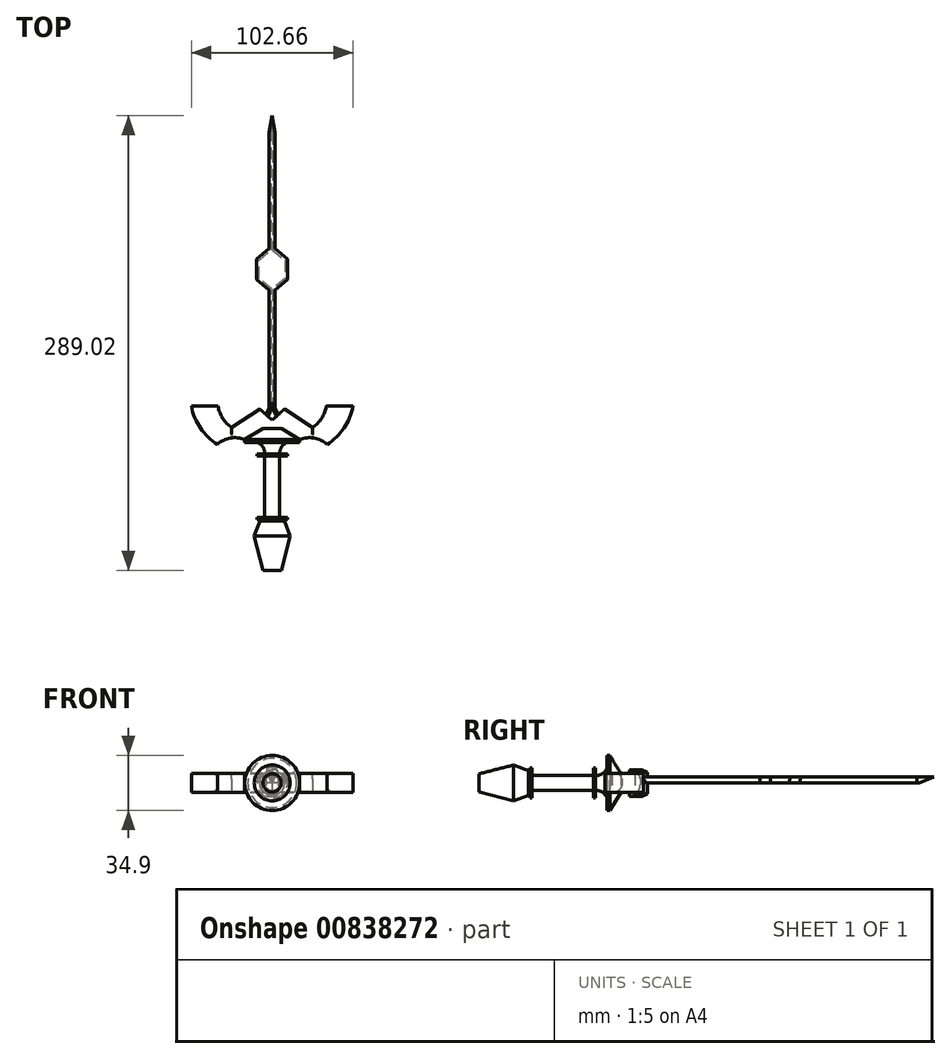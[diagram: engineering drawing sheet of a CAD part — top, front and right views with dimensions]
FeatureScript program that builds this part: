
annotation { "Feature Type Name" : "Feature", "Feature Type Description" : "" }
export const myFeature = defineFeature(function(context is Context, id is Id, definition is map)
    precondition{}
    {
        {
            var Q0;
            Q0=qCreatedBy(makeId("Top.planeOp"),FACE);
            var sketch = newSketch(context, id + "F0", { "sketchPlane" : qUnion([Q0])});
            skLineSegment(sketch, "E0", {"start": v(-11.37, -34.16) * mm, "end": v(-5.8, -56.21) * mm});
            skLineSegment(sketch, "E1", {"start": v(-5.8, -56.21) * mm, "end": v(0, -56.21) * mm});
            skLineSegment(sketch, "E2", {"start": v(-11.37, -34.16) * mm, "end": v(-7.82, -24.78) * mm});
            skLineSegment(sketch, "E3", {"start": v(-7.82, -24.78) * mm, "end": v(0, -24.78) * mm});
            skLineSegment(sketch, "E4", {"start": v(0, -24.78) * mm, "end": v(0, -56.21) * mm});
            skLineSegment(sketch, "E5", {"start": v(-11.37, -34.16) * mm, "end": v(0, -34.16) * mm});
            skLineSegment(sketch, "E6.top", {"start": v(-7.82, -23.73) * mm, "end": v(0, -23.73) * mm});
            skLineSegment(sketch, "E6.left", {"start": v(-7.82, -24.78) * mm, "end": v(-7.82, -23.73) * mm});
            skLineSegment(sketch, "E6.right", {"start": v(0, -24.78) * mm, "end": v(0, -23.73) * mm});
            skLineSegment(sketch, "E7.bottom", {"start": v(0, -23.73) * mm, "end": v(-9.63, -23.73) * mm});
            skLineSegment(sketch, "E7.top", {"start": v(0, -22.58) * mm, "end": v(-9.63, -22.58) * mm});
            skLineSegment(sketch, "E7.left", {"start": v(0, -23.73) * mm, "end": v(0, -22.58) * mm});
            skLineSegment(sketch, "E7.right", {"start": v(-9.63, -23.73) * mm, "end": v(-9.63, -22.58) * mm});
            skLineSegment(sketch, "E8.bottom", {"start": v(-4.82, -22.58) * mm, "end": v(0, -22.58) * mm});
            skLineSegment(sketch, "E8.top", {"start": v(-4.82, 16.66) * mm, "end": v(0, 16.66) * mm});
            skLineSegment(sketch, "E8.left", {"start": v(-4.82, -22.58) * mm, "end": v(-4.82, 16.66) * mm});
            skLineSegment(sketch, "E8.right", {"start": v(0, -22.58) * mm, "end": v(0, 16.66) * mm});
            skLineSegment(sketch, "E9.bottom", {"start": v(0, 16.66) * mm, "end": v(-9.63, 16.66) * mm});
            skLineSegment(sketch, "E9.top", {"start": v(0, 17.78) * mm, "end": v(-9.63, 17.78) * mm});
            skLineSegment(sketch, "E9.left", {"start": v(0, 16.66) * mm, "end": v(0, 17.78) * mm});
            skLineSegment(sketch, "E9.right", {"start": v(-9.63, 16.66) * mm, "end": v(-9.63, 17.78) * mm});
            skArc(sketch, "E10", {"start": v(-4.82, 17.78) * mm, "mid": v(-5.97, 22.28) * mm, "end": v(-9.63, 25.15) * mm});
            skLineSegment(sketch, "E11", {"start": v(0, 17.78) * mm, "end": v(0, 25.15) * mm});
            skLineSegment(sketch, "E12", {"start": v(0, 25.15) * mm, "end": v(-9.63, 25.15) * mm});
            skLineSegment(sketch, "E13.bottom", {"start": v(0, 25.15) * mm, "end": v(-17.45, 25.15) * mm});
            skLineSegment(sketch, "E13.top", {"start": v(0, 26.88) * mm, "end": v(-17.45, 26.88) * mm});
            skLineSegment(sketch, "E13.left", {"start": v(0, 25.15) * mm, "end": v(0, 26.88) * mm});
            skLineSegment(sketch, "E13.right", {"start": v(-17.45, 25.15) * mm, "end": v(-17.45, 26.88) * mm});
            skLineSegment(sketch, "E14", {"start": v(-5.94, 34.05) * mm, "end": v(0, 34.05) * mm});
            skLineSegment(sketch, "E15", {"start": v(0, 34.05) * mm, "end": v(0, 26.88) * mm});
            skArc(sketch, "E16", {"start": v(-17.45, 26.88) * mm, "mid": v(-26.6, 27.93) * mm, "end": v(-34.83, 23.84) * mm});
            skArc(sketch, "E17", {"start": v(-51.33, 48.17) * mm, "mid": v(-45.6, 34.3) * mm, "end": v(-34.83, 23.84) * mm});
            skLineSegment(sketch, "E18", {"start": v(-51.33, 48.17) * mm, "end": v(-34.4, 48.17) * mm});
            skArc(sketch, "E19", {"start": v(-34.4, 48.17) * mm, "mid": v(-31.41, 40.46) * mm, "end": v(-25.7, 34.49) * mm});
            skLineSegment(sketch, "E20", {"start": v(-25.7, 34.49) * mm, "end": v(-7.68, 46.21) * mm});
            skLineSegment(sketch, "E21", {"start": v(-7.68, 46.21) * mm, "end": v(0, 39.26) * mm});
            skLineSegment(sketch, "E22.MirrorCS", {"start": v(7.68, 46.21) * mm, "end": v(0, 39.26) * mm});
            skLineSegment(sketch, "E23.MirrorCS", {"start": v(25.7, 34.49) * mm, "end": v(7.68, 46.21) * mm});
            skLineSegment(sketch, "E24.MirrorCS", {"start": v(5.94, 34.05) * mm, "end": v(0, 34.05) * mm});
            skArc(sketch, "E25.MirrorCS", {"start": v(17.45, 26.88) * mm, "mid": v(26.6, 27.93) * mm, "end": v(34.83, 23.84) * mm});
            skArc(sketch, "E26.MirrorCS", {"start": v(51.33, 48.17) * mm, "mid": v(45.6, 34.3) * mm, "end": v(34.83, 23.84) * mm});
            skLineSegment(sketch, "E27.MirrorCS", {"start": v(51.33, 48.17) * mm, "end": v(34.4, 48.17) * mm});
            skArc(sketch, "E28.MirrorCS", {"start": v(34.4, 48.17) * mm, "mid": v(31.41, 40.46) * mm, "end": v(25.7, 34.49) * mm});
            skLineSegment(sketch, "E29", {"start": v(-7.68, 46.21) * mm, "end": v(-7.68, 119.1) * mm});
            skLineSegment(sketch, "E30", {"start": v(7.68, 46.21) * mm, "end": v(7.68, 119.1) * mm});
            skLineSegment(sketch, "E31", {"start": v(-7.68, 119.1) * mm, "end": v(-15.66, 125.77) * mm});
            skLineSegment(sketch, "E32", {"start": v(-15.66, 125.77) * mm, "end": v(-15.66, 144.25) * mm});
            skLineSegment(sketch, "E33", {"start": v(-15.66, 144.25) * mm, "end": v(-7.68, 150.92) * mm});
            skLineSegment(sketch, "E34", {"start": v(-7.68, 150.92) * mm, "end": v(-7.68, 222.52) * mm});
            skLineSegment(sketch, "E35", {"start": v(-7.68, 222.52) * mm, "end": v(0, 267.13) * mm});
            skLineSegment(sketch, "E36.MirrorCS", {"start": v(7.68, 119.1) * mm, "end": v(15.66, 125.77) * mm});
            skLineSegment(sketch, "E37.MirrorCS", {"start": v(15.66, 125.77) * mm, "end": v(15.66, 144.25) * mm});
            skLineSegment(sketch, "E38.MirrorCS", {"start": v(15.66, 144.25) * mm, "end": v(7.68, 150.92) * mm});
            skLineSegment(sketch, "E39.MirrorCS", {"start": v(7.68, 150.92) * mm, "end": v(7.68, 222.52) * mm});
            skLineSegment(sketch, "E40.MirrorCS", {"start": v(7.68, 222.52) * mm, "end": v(0, 267.13) * mm});
            skLineSegment(sketch, "E41", {"start": v(-5.94, 34.05) * mm, "end": v(-15.55, 26.88) * mm});
            skLineSegment(sketch, "E42.MirrorCS", {"start": v(5.94, 34.05) * mm, "end": v(15.55, 26.88) * mm});
            skLineSegment(sketch, "E43", {"start": v(15.55, 26.88) * mm, "end": v(17.45, 26.88) * mm});
            skLineSegment(sketch, "E44", {"start": v(-5.94, 34.05) * mm, "end": v(-17.45, 26.88) * mm});
            skLineSegment(sketch, "E45", {"start": v(5.94, 34.05) * mm, "end": v(17.45, 26.88) * mm});
            skLineSegment(sketch, "E46", {"start": v(-3.84, 42.74) * mm, "end": v(0, 50.69) * mm});
            skLineSegment(sketch, "E47", {"start": v(0, 50.69) * mm, "end": v(3.84, 42.74) * mm});
            skLineSegment(sketch, "E48", {"start": v(0, 50.69) * mm, "end": v(0, 39.26) * mm});
            skLineSegment(sketch, "E49", {"start": v(-3.84, 42.74) * mm, "end": v(3.84, 42.74) * mm});
            skSolve(sketch);
        }
        {
            var Q0;
            Q0=makeQuery(id+"F0.imprint","IMPRINT",FACE,{"disambiguationData":[TD([[makeQuery(id+"F0.imprint","IMPRINT",EDGE,{"derivedFrom":sQuery(id+"F0.wireOp",EDGE,"E0")}),1.0]])]});
            var Q1;
            Q1=makeQuery(id+"F0.imprint","IMPRINT",FACE,{"disambiguationData":[TD([[makeQuery(id+"F0.imprint","IMPRINT",EDGE,{"derivedFrom":sQuery(id+"F0.wireOp",EDGE,"E2")}),-1.0]])]});
            var Q2;
            Q2=makeQuery(id+"F0.imprint","IMPRINT",FACE,{"disambiguationData":[TD([[makeQuery(id+"F0.imprint","IMPRINT",EDGE,{"derivedFrom":sQuery(id+"F0.wireOp",EDGE,"E3")}),1.0]])]});
            var Q3;
            Q3=makeQuery(id+"F0.imprint","IMPRINT",FACE,{"disambiguationData":[TD([[makeQuery(id+"F0.imprint","IMPRINT",EDGE,{"derivedFrom":sQuery(id+"F0.wireOp",EDGE,"E6.top")}),1.0]])]});
            var Q4;
            Q4=makeQuery(id+"F0.imprint","IMPRINT",FACE,{"disambiguationData":[TD([[makeQuery(id+"F0.imprint","IMPRINT",EDGE,{"derivedFrom":sQuery(id+"F0.wireOp",EDGE,"E8.top")}),-1.0]])]});
            var Q5;
            Q5=makeQuery(id+"F0.imprint","IMPRINT",FACE,{"disambiguationData":[TD([[makeQuery(id+"F0.imprint","IMPRINT",EDGE,{"derivedFrom":sQuery(id+"F0.wireOp",EDGE,"E8.top")}),1.0]])]});
            var Q6;
            {var subQ0=sQuery(id+"F0.wireOp",EDGE,"E10");Q6=makeQuery(id+"F0.imprint","IMPRINT",FACE,{"disambiguationData":[TD([[makeQuery(id+"F0.imprint","IMPRINT",EDGE,{"derivedFrom":subQ0}),-1.0]])]});}
            var Q7;
            Q7=makeQuery(id+"F0.imprint","IMPRINT",FACE,{"disambiguationData":[TD([[makeQuery(id+"F0.imprint","IMPRINT",EDGE,{"derivedFrom":sQuery(id+"F0.wireOp",EDGE,"E12")}),-1.0]])]});
            var Q8;
            {var subQ2=sQuery(id+"F0.wireOp",EDGE,"E41");Q8=makeQuery(id+"F0.imprint","IMPRINT",FACE,{"disambiguationData":[TD([[makeQuery(id+"F0.imprint","IMPRINT",EDGE,{"derivedFrom":subQ2}),-1.0]])]});}
            var Q9;
            Q9=sQuery(id+"F0.wireOp",EDGE,"E4");
            revolve(context, id + "F1", {"surfaceOperationType" : NewSurfaceOperationType.NEW, "entities" : qUnion([Q0, Q1, Q2, Q3, Q4, Q5, Q6, Q7, Q8]), "axis" : qUnion([Q9]), "revolveType" : RevolveType.FULL});
        }
        {
            var Q0;
            Q0=makeQuery(id+"F0.imprint","IMPRINT",FACE,{"disambiguationData":[TD([[makeQuery(id+"F0.imprint","IMPRINT",EDGE,{"derivedFrom":sQuery(id+"F0.wireOp",EDGE,"E14")}),1.0]])]});
            extrude(context, id + "F2", {"entities" : qUnion([Q0]), "endBound" : BoundingType.SYMMETRIC, "depth" : 12.2 * mm, "offsetDistance" : 25.4 * mm});
        }
        {
            var Q0;
            {var subQ0=sQuery(id+"F0.wireOp",EDGE,"E48");var subQ3=sQuery(id+"F0.wireOp",EDGE,"E49");var subQ5=makeQuery(id+"F0.imprint","INTERSECT",VERTEX,{"derivedFrom":[subQ0,subQ3]});Q0=makeQuery(id+"F0.imprint","IMPRINT",FACE,{"disambiguationData":[TD([[makeQuery(id+"F0.imprint","IMPRINT",EDGE,{"disambiguationData":[TD([[subQ5,-1.0]])],"derivedFrom":subQ0}),-1.0]])]});}
            var Q1;
            {var subQ0=sQuery(id+"F0.wireOp",EDGE,"E47");Q1=makeQuery(id+"F0.imprint","IMPRINT",FACE,{"disambiguationData":[TD([[makeQuery(id+"F0.imprint","IMPRINT",EDGE,{"derivedFrom":subQ0}),-1.0]])]});}
            var Q2;
            {var subQ0=sQuery(id+"F0.wireOp",EDGE,"E48");var subQ3=sQuery(id+"F0.wireOp",EDGE,"E49");var subQ5=makeQuery(id+"F0.imprint","INTERSECT",VERTEX,{"derivedFrom":[subQ0,subQ3]});Q2=makeQuery(id+"F0.imprint","IMPRINT",FACE,{"disambiguationData":[TD([[makeQuery(id+"F0.imprint","IMPRINT",EDGE,{"disambiguationData":[TD([[subQ5,-1.0]])],"derivedFrom":subQ0}),1.0]])]});}
            var Q3;
            {var subQ0=sQuery(id+"F0.wireOp",EDGE,"E46");Q3=makeQuery(id+"F0.imprint","IMPRINT",FACE,{"disambiguationData":[TD([[makeQuery(id+"F0.imprint","IMPRINT",EDGE,{"derivedFrom":subQ0}),-1.0]])]});}
            extrude(context, id + "F3", {"entities" : qUnion([Q0, Q1, Q2, Q3]), "operationType" : NewBodyOperationType.ADD, "endBound" : BoundingType.SYMMETRIC, "depth" : 16.76 * mm, "offsetDistance" : 25.4 * mm});
        }
        {
            var Q0;
            Q0=makeQuery(id+"F3.opExtrude","CAP_EDGE",EDGE,{"disambiguationData":[OSD([sQuery(id+"F0.wireOp",EDGE,"E46")])],"isStart":false});
            var Q1;
            Q1=makeQuery(id+"F3.opExtrude","CAP_EDGE",EDGE,{"disambiguationData":[OSD([sQuery(id+"F0.wireOp",EDGE,"E47")])],"isStart":false});
            chamfer(context, id + "F4", {"entities" : qUnion([Q0, Q1]), "width" : 1.52 * mm, "tangentPropagation" : true});
        }
        {
            var Q0;
            {var subQ0=sQuery(id+"F0.wireOp",EDGE,"E29");Q0=makeQuery(id+"F0.imprint","IMPRINT",FACE,{"disambiguationData":[TD([[makeQuery(id+"F0.imprint","IMPRINT",EDGE,{"derivedFrom":subQ0}),-1.0]])]});}
            extrude(context, id + "F5", {"entities" : qUnion([Q0]), "operationType" : NewBodyOperationType.ADD, "depth" : 3.8 * mm, "offsetDistance" : 25.4 * mm});
        }
        {
            var Q0;
            Q0=makeQuery(id+"F5.opExtrude","CAP_EDGE",EDGE,{"disambiguationData":[OSD([sQuery(id+"F0.wireOp",EDGE,"E35")])],"isStart":false});
            var Q1;
            Q1=makeQuery(id+"F5.opExtrude","CAP_EDGE",EDGE,{"disambiguationData":[OSD([sQuery(id+"F0.wireOp",EDGE,"E40.MirrorCS")])],"isStart":false});
            var Q2;
            Q2=makeQuery(id+"F5.opExtrude","CAP_EDGE",EDGE,{"disambiguationData":[OSD([sQuery(id+"F0.wireOp",EDGE,"E34")])],"isStart":false});
            var Q3;
            Q3=makeQuery(id+"F5.opExtrude","CAP_EDGE",EDGE,{"disambiguationData":[OSD([sQuery(id+"F0.wireOp",EDGE,"E39.MirrorCS")])],"isStart":false});
            var Q4;
            Q4=makeQuery(id+"F5.opExtrude","CAP_EDGE",EDGE,{"disambiguationData":[OSD([sQuery(id+"F0.wireOp",EDGE,"E33")])],"isStart":false});
            var Q5;
            Q5=makeQuery(id+"F5.opExtrude","CAP_EDGE",EDGE,{"disambiguationData":[OSD([sQuery(id+"F0.wireOp",EDGE,"E32")])],"isStart":false});
            var Q6;
            Q6=makeQuery(id+"F5.opExtrude","CAP_EDGE",EDGE,{"disambiguationData":[OSD([sQuery(id+"F0.wireOp",EDGE,"E31")])],"isStart":false});
            var Q7;
            Q7=makeQuery(id+"F5.opExtrude","CAP_EDGE",EDGE,{"disambiguationData":[OSD([sQuery(id+"F0.wireOp",EDGE,"E29")])],"isStart":false});
            var Q8;
            Q8=makeQuery(id+"F5.opExtrude","CAP_EDGE",EDGE,{"disambiguationData":[OSD([sQuery(id+"F0.wireOp",EDGE,"E30")])],"isStart":false});
            var Q9;
            Q9=makeQuery(id+"F5.opExtrude","CAP_EDGE",EDGE,{"disambiguationData":[OSD([sQuery(id+"F0.wireOp",EDGE,"E36.MirrorCS")])],"isStart":false});
            var Q10;
            Q10=makeQuery(id+"F5.opExtrude","CAP_EDGE",EDGE,{"disambiguationData":[OSD([sQuery(id+"F0.wireOp",EDGE,"E37.MirrorCS")])],"isStart":false});
            var Q11;
            Q11=makeQuery(id+"F5.opExtrude","CAP_EDGE",EDGE,{"disambiguationData":[OSD([sQuery(id+"F0.wireOp",EDGE,"E38.MirrorCS")])],"isStart":false});
            chamfer(context, id + "F6", {"entities" : qUnion([Q0, Q1, Q2, Q3, Q4, Q5, Q6, Q7, Q8, Q9, Q10, Q11]), "width" : 5.08 * mm, "tangentPropagation" : true});
        }
        {
            var Q0;
            {var subQ0=sQuery(id+"F0.wireOp",EDGE,"E37.MirrorCS");Q0=makeQuery(id+"F6.opChamfer","BLEND_EDGE",EDGE,{"blendedFrom":[makeQuery(id+"F5.opExtrude","CAP_EDGE",EDGE,{"disambiguationData":[OSD([subQ0])],"isStart":false}),makeQuery(id+"F5.opExtrude","CAP_FACE",FACE,{"disambiguationData":[OSD([sQuery(id+"F0.wireOp",EDGE,"E21"),sQuery(id+"F0.wireOp",EDGE,"E22.MirrorCS"),sQuery(id+"F0.wireOp",EDGE,"E29"),sQuery(id+"F0.wireOp",EDGE,"E30"),sQuery(id+"F0.wireOp",EDGE,"E31"),sQuery(id+"F0.wireOp",EDGE,"E32"),sQuery(id+"F0.wireOp",EDGE,"E33"),sQuery(id+"F0.wireOp",EDGE,"E34"),sQuery(id+"F0.wireOp",EDGE,"E35"),sQuery(id+"F0.wireOp",EDGE,"E36.MirrorCS"),subQ0,sQuery(id+"F0.wireOp",EDGE,"E38.MirrorCS"),sQuery(id+"F0.wireOp",EDGE,"E39.MirrorCS"),sQuery(id+"F0.wireOp",EDGE,"E40.MirrorCS"),sQuery(id+"F0.wireOp",EDGE,"E46"),sQuery(id+"F0.wireOp",EDGE,"E47")])],"isStart":true})],"blendedInto":[makeQuery(id+"F5.opExtrude","CAP_FACE",FACE,{"disambiguationData":[OSD([sQuery(id+"F0.wireOp",EDGE,"E21"),sQuery(id+"F0.wireOp",EDGE,"E22.MirrorCS"),sQuery(id+"F0.wireOp",EDGE,"E29"),sQuery(id+"F0.wireOp",EDGE,"E30"),sQuery(id+"F0.wireOp",EDGE,"E31"),sQuery(id+"F0.wireOp",EDGE,"E32"),sQuery(id+"F0.wireOp",EDGE,"E33"),sQuery(id+"F0.wireOp",EDGE,"E34"),sQuery(id+"F0.wireOp",EDGE,"E35"),sQuery(id+"F0.wireOp",EDGE,"E36.MirrorCS"),subQ0,sQuery(id+"F0.wireOp",EDGE,"E38.MirrorCS"),sQuery(id+"F0.wireOp",EDGE,"E39.MirrorCS"),sQuery(id+"F0.wireOp",EDGE,"E40.MirrorCS"),sQuery(id+"F0.wireOp",EDGE,"E46"),sQuery(id+"F0.wireOp",EDGE,"E47")])],"isStart":true})]});}
            var Q1;
            {var subQ0=sQuery(id+"F0.wireOp",EDGE,"E36.MirrorCS");Q1=makeQuery(id+"F6.opChamfer","BLEND_EDGE",EDGE,{"blendedFrom":[makeQuery(id+"F5.opExtrude","CAP_EDGE",EDGE,{"disambiguationData":[OSD([subQ0])],"isStart":false}),makeQuery(id+"F5.opExtrude","CAP_FACE",FACE,{"disambiguationData":[OSD([sQuery(id+"F0.wireOp",EDGE,"E21"),sQuery(id+"F0.wireOp",EDGE,"E22.MirrorCS"),sQuery(id+"F0.wireOp",EDGE,"E29"),sQuery(id+"F0.wireOp",EDGE,"E30"),sQuery(id+"F0.wireOp",EDGE,"E31"),sQuery(id+"F0.wireOp",EDGE,"E32"),sQuery(id+"F0.wireOp",EDGE,"E33"),sQuery(id+"F0.wireOp",EDGE,"E34"),sQuery(id+"F0.wireOp",EDGE,"E35"),subQ0,sQuery(id+"F0.wireOp",EDGE,"E37.MirrorCS"),sQuery(id+"F0.wireOp",EDGE,"E38.MirrorCS"),sQuery(id+"F0.wireOp",EDGE,"E39.MirrorCS"),sQuery(id+"F0.wireOp",EDGE,"E40.MirrorCS"),sQuery(id+"F0.wireOp",EDGE,"E46"),sQuery(id+"F0.wireOp",EDGE,"E47")])],"isStart":true})],"blendedInto":[makeQuery(id+"F5.opExtrude","CAP_FACE",FACE,{"disambiguationData":[OSD([sQuery(id+"F0.wireOp",EDGE,"E21"),sQuery(id+"F0.wireOp",EDGE,"E22.MirrorCS"),sQuery(id+"F0.wireOp",EDGE,"E29"),sQuery(id+"F0.wireOp",EDGE,"E30"),sQuery(id+"F0.wireOp",EDGE,"E31"),sQuery(id+"F0.wireOp",EDGE,"E32"),sQuery(id+"F0.wireOp",EDGE,"E33"),sQuery(id+"F0.wireOp",EDGE,"E34"),sQuery(id+"F0.wireOp",EDGE,"E35"),subQ0,sQuery(id+"F0.wireOp",EDGE,"E37.MirrorCS"),sQuery(id+"F0.wireOp",EDGE,"E38.MirrorCS"),sQuery(id+"F0.wireOp",EDGE,"E39.MirrorCS"),sQuery(id+"F0.wireOp",EDGE,"E40.MirrorCS"),sQuery(id+"F0.wireOp",EDGE,"E46"),sQuery(id+"F0.wireOp",EDGE,"E47")])],"isStart":true})]});}
            var Q2;
            {var subQ0=sQuery(id+"F0.wireOp",EDGE,"E38.MirrorCS");Q2=makeQuery(id+"F6.opChamfer","BLEND_EDGE",EDGE,{"blendedFrom":[makeQuery(id+"F5.opExtrude","CAP_EDGE",EDGE,{"disambiguationData":[OSD([subQ0])],"isStart":false}),makeQuery(id+"F5.opExtrude","CAP_FACE",FACE,{"disambiguationData":[OSD([sQuery(id+"F0.wireOp",EDGE,"E21"),sQuery(id+"F0.wireOp",EDGE,"E22.MirrorCS"),sQuery(id+"F0.wireOp",EDGE,"E29"),sQuery(id+"F0.wireOp",EDGE,"E30"),sQuery(id+"F0.wireOp",EDGE,"E31"),sQuery(id+"F0.wireOp",EDGE,"E32"),sQuery(id+"F0.wireOp",EDGE,"E33"),sQuery(id+"F0.wireOp",EDGE,"E34"),sQuery(id+"F0.wireOp",EDGE,"E35"),sQuery(id+"F0.wireOp",EDGE,"E36.MirrorCS"),sQuery(id+"F0.wireOp",EDGE,"E37.MirrorCS"),subQ0,sQuery(id+"F0.wireOp",EDGE,"E39.MirrorCS"),sQuery(id+"F0.wireOp",EDGE,"E40.MirrorCS"),sQuery(id+"F0.wireOp",EDGE,"E46"),sQuery(id+"F0.wireOp",EDGE,"E47")])],"isStart":true})],"blendedInto":[makeQuery(id+"F5.opExtrude","CAP_FACE",FACE,{"disambiguationData":[OSD([sQuery(id+"F0.wireOp",EDGE,"E21"),sQuery(id+"F0.wireOp",EDGE,"E22.MirrorCS"),sQuery(id+"F0.wireOp",EDGE,"E29"),sQuery(id+"F0.wireOp",EDGE,"E30"),sQuery(id+"F0.wireOp",EDGE,"E31"),sQuery(id+"F0.wireOp",EDGE,"E32"),sQuery(id+"F0.wireOp",EDGE,"E33"),sQuery(id+"F0.wireOp",EDGE,"E34"),sQuery(id+"F0.wireOp",EDGE,"E35"),sQuery(id+"F0.wireOp",EDGE,"E36.MirrorCS"),sQuery(id+"F0.wireOp",EDGE,"E37.MirrorCS"),subQ0,sQuery(id+"F0.wireOp",EDGE,"E39.MirrorCS"),sQuery(id+"F0.wireOp",EDGE,"E40.MirrorCS"),sQuery(id+"F0.wireOp",EDGE,"E46"),sQuery(id+"F0.wireOp",EDGE,"E47")])],"isStart":true})]});}
            var Q3;
            {var subQ0=sQuery(id+"F0.wireOp",EDGE,"E32");Q3=makeQuery(id+"F6.opChamfer","BLEND_EDGE",EDGE,{"blendedFrom":[makeQuery(id+"F5.opExtrude","CAP_EDGE",EDGE,{"disambiguationData":[OSD([subQ0])],"isStart":false}),makeQuery(id+"F5.opExtrude","CAP_FACE",FACE,{"disambiguationData":[OSD([sQuery(id+"F0.wireOp",EDGE,"E21"),sQuery(id+"F0.wireOp",EDGE,"E22.MirrorCS"),sQuery(id+"F0.wireOp",EDGE,"E29"),sQuery(id+"F0.wireOp",EDGE,"E30"),sQuery(id+"F0.wireOp",EDGE,"E31"),subQ0,sQuery(id+"F0.wireOp",EDGE,"E33"),sQuery(id+"F0.wireOp",EDGE,"E34"),sQuery(id+"F0.wireOp",EDGE,"E35"),sQuery(id+"F0.wireOp",EDGE,"E36.MirrorCS"),sQuery(id+"F0.wireOp",EDGE,"E37.MirrorCS"),sQuery(id+"F0.wireOp",EDGE,"E38.MirrorCS"),sQuery(id+"F0.wireOp",EDGE,"E39.MirrorCS"),sQuery(id+"F0.wireOp",EDGE,"E40.MirrorCS"),sQuery(id+"F0.wireOp",EDGE,"E46"),sQuery(id+"F0.wireOp",EDGE,"E47")])],"isStart":true})],"blendedInto":[makeQuery(id+"F5.opExtrude","CAP_FACE",FACE,{"disambiguationData":[OSD([sQuery(id+"F0.wireOp",EDGE,"E21"),sQuery(id+"F0.wireOp",EDGE,"E22.MirrorCS"),sQuery(id+"F0.wireOp",EDGE,"E29"),sQuery(id+"F0.wireOp",EDGE,"E30"),sQuery(id+"F0.wireOp",EDGE,"E31"),subQ0,sQuery(id+"F0.wireOp",EDGE,"E33"),sQuery(id+"F0.wireOp",EDGE,"E34"),sQuery(id+"F0.wireOp",EDGE,"E35"),sQuery(id+"F0.wireOp",EDGE,"E36.MirrorCS"),sQuery(id+"F0.wireOp",EDGE,"E37.MirrorCS"),sQuery(id+"F0.wireOp",EDGE,"E38.MirrorCS"),sQuery(id+"F0.wireOp",EDGE,"E39.MirrorCS"),sQuery(id+"F0.wireOp",EDGE,"E40.MirrorCS"),sQuery(id+"F0.wireOp",EDGE,"E46"),sQuery(id+"F0.wireOp",EDGE,"E47")])],"isStart":true})]});}
            var Q4;
            {var subQ0=sQuery(id+"F0.wireOp",EDGE,"E33");Q4=makeQuery(id+"F6.opChamfer","BLEND_EDGE",EDGE,{"blendedFrom":[makeQuery(id+"F5.opExtrude","CAP_EDGE",EDGE,{"disambiguationData":[OSD([subQ0])],"isStart":false}),makeQuery(id+"F5.opExtrude","CAP_FACE",FACE,{"disambiguationData":[OSD([sQuery(id+"F0.wireOp",EDGE,"E21"),sQuery(id+"F0.wireOp",EDGE,"E22.MirrorCS"),sQuery(id+"F0.wireOp",EDGE,"E29"),sQuery(id+"F0.wireOp",EDGE,"E30"),sQuery(id+"F0.wireOp",EDGE,"E31"),sQuery(id+"F0.wireOp",EDGE,"E32"),subQ0,sQuery(id+"F0.wireOp",EDGE,"E34"),sQuery(id+"F0.wireOp",EDGE,"E35"),sQuery(id+"F0.wireOp",EDGE,"E36.MirrorCS"),sQuery(id+"F0.wireOp",EDGE,"E37.MirrorCS"),sQuery(id+"F0.wireOp",EDGE,"E38.MirrorCS"),sQuery(id+"F0.wireOp",EDGE,"E39.MirrorCS"),sQuery(id+"F0.wireOp",EDGE,"E40.MirrorCS"),sQuery(id+"F0.wireOp",EDGE,"E46"),sQuery(id+"F0.wireOp",EDGE,"E47")])],"isStart":true})],"blendedInto":[makeQuery(id+"F5.opExtrude","CAP_FACE",FACE,{"disambiguationData":[OSD([sQuery(id+"F0.wireOp",EDGE,"E21"),sQuery(id+"F0.wireOp",EDGE,"E22.MirrorCS"),sQuery(id+"F0.wireOp",EDGE,"E29"),sQuery(id+"F0.wireOp",EDGE,"E30"),sQuery(id+"F0.wireOp",EDGE,"E31"),sQuery(id+"F0.wireOp",EDGE,"E32"),subQ0,sQuery(id+"F0.wireOp",EDGE,"E34"),sQuery(id+"F0.wireOp",EDGE,"E35"),sQuery(id+"F0.wireOp",EDGE,"E36.MirrorCS"),sQuery(id+"F0.wireOp",EDGE,"E37.MirrorCS"),sQuery(id+"F0.wireOp",EDGE,"E38.MirrorCS"),sQuery(id+"F0.wireOp",EDGE,"E39.MirrorCS"),sQuery(id+"F0.wireOp",EDGE,"E40.MirrorCS"),sQuery(id+"F0.wireOp",EDGE,"E46"),sQuery(id+"F0.wireOp",EDGE,"E47")])],"isStart":true})]});}
            var Q5;
            {var subQ0=sQuery(id+"F0.wireOp",EDGE,"E31");Q5=makeQuery(id+"F6.opChamfer","BLEND_EDGE",EDGE,{"blendedFrom":[makeQuery(id+"F5.opExtrude","CAP_EDGE",EDGE,{"disambiguationData":[OSD([subQ0])],"isStart":false}),makeQuery(id+"F5.opExtrude","CAP_FACE",FACE,{"disambiguationData":[OSD([sQuery(id+"F0.wireOp",EDGE,"E21"),sQuery(id+"F0.wireOp",EDGE,"E22.MirrorCS"),sQuery(id+"F0.wireOp",EDGE,"E29"),sQuery(id+"F0.wireOp",EDGE,"E30"),subQ0,sQuery(id+"F0.wireOp",EDGE,"E32"),sQuery(id+"F0.wireOp",EDGE,"E33"),sQuery(id+"F0.wireOp",EDGE,"E34"),sQuery(id+"F0.wireOp",EDGE,"E35"),sQuery(id+"F0.wireOp",EDGE,"E36.MirrorCS"),sQuery(id+"F0.wireOp",EDGE,"E37.MirrorCS"),sQuery(id+"F0.wireOp",EDGE,"E38.MirrorCS"),sQuery(id+"F0.wireOp",EDGE,"E39.MirrorCS"),sQuery(id+"F0.wireOp",EDGE,"E40.MirrorCS"),sQuery(id+"F0.wireOp",EDGE,"E46"),sQuery(id+"F0.wireOp",EDGE,"E47")])],"isStart":true})],"blendedInto":[makeQuery(id+"F5.opExtrude","CAP_FACE",FACE,{"disambiguationData":[OSD([sQuery(id+"F0.wireOp",EDGE,"E21"),sQuery(id+"F0.wireOp",EDGE,"E22.MirrorCS"),sQuery(id+"F0.wireOp",EDGE,"E29"),sQuery(id+"F0.wireOp",EDGE,"E30"),subQ0,sQuery(id+"F0.wireOp",EDGE,"E32"),sQuery(id+"F0.wireOp",EDGE,"E33"),sQuery(id+"F0.wireOp",EDGE,"E34"),sQuery(id+"F0.wireOp",EDGE,"E35"),sQuery(id+"F0.wireOp",EDGE,"E36.MirrorCS"),sQuery(id+"F0.wireOp",EDGE,"E37.MirrorCS"),sQuery(id+"F0.wireOp",EDGE,"E38.MirrorCS"),sQuery(id+"F0.wireOp",EDGE,"E39.MirrorCS"),sQuery(id+"F0.wireOp",EDGE,"E40.MirrorCS"),sQuery(id+"F0.wireOp",EDGE,"E46"),sQuery(id+"F0.wireOp",EDGE,"E47")])],"isStart":true})]});}
            var Q6;
            {var subQ0=sQuery(id+"F0.wireOp",EDGE,"E30");Q6=makeQuery(id+"F6.opChamfer","BLEND_EDGE",EDGE,{"blendedFrom":[makeQuery(id+"F5.opExtrude","CAP_EDGE",EDGE,{"disambiguationData":[OSD([subQ0])],"isStart":false}),makeQuery(id+"F5.opExtrude","CAP_FACE",FACE,{"disambiguationData":[OSD([sQuery(id+"F0.wireOp",EDGE,"E21"),sQuery(id+"F0.wireOp",EDGE,"E22.MirrorCS"),sQuery(id+"F0.wireOp",EDGE,"E29"),subQ0,sQuery(id+"F0.wireOp",EDGE,"E31"),sQuery(id+"F0.wireOp",EDGE,"E32"),sQuery(id+"F0.wireOp",EDGE,"E33"),sQuery(id+"F0.wireOp",EDGE,"E34"),sQuery(id+"F0.wireOp",EDGE,"E35"),sQuery(id+"F0.wireOp",EDGE,"E36.MirrorCS"),sQuery(id+"F0.wireOp",EDGE,"E37.MirrorCS"),sQuery(id+"F0.wireOp",EDGE,"E38.MirrorCS"),sQuery(id+"F0.wireOp",EDGE,"E39.MirrorCS"),sQuery(id+"F0.wireOp",EDGE,"E40.MirrorCS"),sQuery(id+"F0.wireOp",EDGE,"E46"),sQuery(id+"F0.wireOp",EDGE,"E47")])],"isStart":true})],"blendedInto":[makeQuery(id+"F5.opExtrude","CAP_FACE",FACE,{"disambiguationData":[OSD([sQuery(id+"F0.wireOp",EDGE,"E21"),sQuery(id+"F0.wireOp",EDGE,"E22.MirrorCS"),sQuery(id+"F0.wireOp",EDGE,"E29"),subQ0,sQuery(id+"F0.wireOp",EDGE,"E31"),sQuery(id+"F0.wireOp",EDGE,"E32"),sQuery(id+"F0.wireOp",EDGE,"E33"),sQuery(id+"F0.wireOp",EDGE,"E34"),sQuery(id+"F0.wireOp",EDGE,"E35"),sQuery(id+"F0.wireOp",EDGE,"E36.MirrorCS"),sQuery(id+"F0.wireOp",EDGE,"E37.MirrorCS"),sQuery(id+"F0.wireOp",EDGE,"E38.MirrorCS"),sQuery(id+"F0.wireOp",EDGE,"E39.MirrorCS"),sQuery(id+"F0.wireOp",EDGE,"E40.MirrorCS"),sQuery(id+"F0.wireOp",EDGE,"E46"),sQuery(id+"F0.wireOp",EDGE,"E47")])],"isStart":true})]});}
            var Q7;
            {var subQ0=sQuery(id+"F0.wireOp",EDGE,"E29");Q7=makeQuery(id+"F6.opChamfer","BLEND_EDGE",EDGE,{"blendedFrom":[makeQuery(id+"F5.opExtrude","CAP_EDGE",EDGE,{"disambiguationData":[OSD([subQ0])],"isStart":false}),makeQuery(id+"F5.opExtrude","CAP_FACE",FACE,{"disambiguationData":[OSD([sQuery(id+"F0.wireOp",EDGE,"E21"),sQuery(id+"F0.wireOp",EDGE,"E22.MirrorCS"),subQ0,sQuery(id+"F0.wireOp",EDGE,"E30"),sQuery(id+"F0.wireOp",EDGE,"E31"),sQuery(id+"F0.wireOp",EDGE,"E32"),sQuery(id+"F0.wireOp",EDGE,"E33"),sQuery(id+"F0.wireOp",EDGE,"E34"),sQuery(id+"F0.wireOp",EDGE,"E35"),sQuery(id+"F0.wireOp",EDGE,"E36.MirrorCS"),sQuery(id+"F0.wireOp",EDGE,"E37.MirrorCS"),sQuery(id+"F0.wireOp",EDGE,"E38.MirrorCS"),sQuery(id+"F0.wireOp",EDGE,"E39.MirrorCS"),sQuery(id+"F0.wireOp",EDGE,"E40.MirrorCS"),sQuery(id+"F0.wireOp",EDGE,"E46"),sQuery(id+"F0.wireOp",EDGE,"E47")])],"isStart":true})],"blendedInto":[makeQuery(id+"F5.opExtrude","CAP_FACE",FACE,{"disambiguationData":[OSD([sQuery(id+"F0.wireOp",EDGE,"E21"),sQuery(id+"F0.wireOp",EDGE,"E22.MirrorCS"),subQ0,sQuery(id+"F0.wireOp",EDGE,"E30"),sQuery(id+"F0.wireOp",EDGE,"E31"),sQuery(id+"F0.wireOp",EDGE,"E32"),sQuery(id+"F0.wireOp",EDGE,"E33"),sQuery(id+"F0.wireOp",EDGE,"E34"),sQuery(id+"F0.wireOp",EDGE,"E35"),sQuery(id+"F0.wireOp",EDGE,"E36.MirrorCS"),sQuery(id+"F0.wireOp",EDGE,"E37.MirrorCS"),sQuery(id+"F0.wireOp",EDGE,"E38.MirrorCS"),sQuery(id+"F0.wireOp",EDGE,"E39.MirrorCS"),sQuery(id+"F0.wireOp",EDGE,"E40.MirrorCS"),sQuery(id+"F0.wireOp",EDGE,"E46"),sQuery(id+"F0.wireOp",EDGE,"E47")])],"isStart":true})]});}
            var Q8;
            {var subQ0=sQuery(id+"F0.wireOp",EDGE,"E39.MirrorCS");Q8=makeQuery(id+"F6.opChamfer","BLEND_EDGE",EDGE,{"blendedFrom":[makeQuery(id+"F5.opExtrude","CAP_EDGE",EDGE,{"disambiguationData":[OSD([subQ0])],"isStart":false}),makeQuery(id+"F5.opExtrude","CAP_FACE",FACE,{"disambiguationData":[OSD([sQuery(id+"F0.wireOp",EDGE,"E21"),sQuery(id+"F0.wireOp",EDGE,"E22.MirrorCS"),sQuery(id+"F0.wireOp",EDGE,"E29"),sQuery(id+"F0.wireOp",EDGE,"E30"),sQuery(id+"F0.wireOp",EDGE,"E31"),sQuery(id+"F0.wireOp",EDGE,"E32"),sQuery(id+"F0.wireOp",EDGE,"E33"),sQuery(id+"F0.wireOp",EDGE,"E34"),sQuery(id+"F0.wireOp",EDGE,"E35"),sQuery(id+"F0.wireOp",EDGE,"E36.MirrorCS"),sQuery(id+"F0.wireOp",EDGE,"E37.MirrorCS"),sQuery(id+"F0.wireOp",EDGE,"E38.MirrorCS"),subQ0,sQuery(id+"F0.wireOp",EDGE,"E40.MirrorCS"),sQuery(id+"F0.wireOp",EDGE,"E46"),sQuery(id+"F0.wireOp",EDGE,"E47")])],"isStart":true})],"blendedInto":[makeQuery(id+"F5.opExtrude","CAP_FACE",FACE,{"disambiguationData":[OSD([sQuery(id+"F0.wireOp",EDGE,"E21"),sQuery(id+"F0.wireOp",EDGE,"E22.MirrorCS"),sQuery(id+"F0.wireOp",EDGE,"E29"),sQuery(id+"F0.wireOp",EDGE,"E30"),sQuery(id+"F0.wireOp",EDGE,"E31"),sQuery(id+"F0.wireOp",EDGE,"E32"),sQuery(id+"F0.wireOp",EDGE,"E33"),sQuery(id+"F0.wireOp",EDGE,"E34"),sQuery(id+"F0.wireOp",EDGE,"E35"),sQuery(id+"F0.wireOp",EDGE,"E36.MirrorCS"),sQuery(id+"F0.wireOp",EDGE,"E37.MirrorCS"),sQuery(id+"F0.wireOp",EDGE,"E38.MirrorCS"),subQ0,sQuery(id+"F0.wireOp",EDGE,"E40.MirrorCS"),sQuery(id+"F0.wireOp",EDGE,"E46"),sQuery(id+"F0.wireOp",EDGE,"E47")])],"isStart":true})]});}
            var Q9;
            {var subQ0=sQuery(id+"F0.wireOp",EDGE,"E34");Q9=makeQuery(id+"F6.opChamfer","BLEND_EDGE",EDGE,{"blendedFrom":[makeQuery(id+"F5.opExtrude","CAP_EDGE",EDGE,{"disambiguationData":[OSD([subQ0])],"isStart":false}),makeQuery(id+"F5.opExtrude","CAP_FACE",FACE,{"disambiguationData":[OSD([sQuery(id+"F0.wireOp",EDGE,"E21"),sQuery(id+"F0.wireOp",EDGE,"E22.MirrorCS"),sQuery(id+"F0.wireOp",EDGE,"E29"),sQuery(id+"F0.wireOp",EDGE,"E30"),sQuery(id+"F0.wireOp",EDGE,"E31"),sQuery(id+"F0.wireOp",EDGE,"E32"),sQuery(id+"F0.wireOp",EDGE,"E33"),subQ0,sQuery(id+"F0.wireOp",EDGE,"E35"),sQuery(id+"F0.wireOp",EDGE,"E36.MirrorCS"),sQuery(id+"F0.wireOp",EDGE,"E37.MirrorCS"),sQuery(id+"F0.wireOp",EDGE,"E38.MirrorCS"),sQuery(id+"F0.wireOp",EDGE,"E39.MirrorCS"),sQuery(id+"F0.wireOp",EDGE,"E40.MirrorCS"),sQuery(id+"F0.wireOp",EDGE,"E46"),sQuery(id+"F0.wireOp",EDGE,"E47")])],"isStart":true})],"blendedInto":[makeQuery(id+"F5.opExtrude","CAP_FACE",FACE,{"disambiguationData":[OSD([sQuery(id+"F0.wireOp",EDGE,"E21"),sQuery(id+"F0.wireOp",EDGE,"E22.MirrorCS"),sQuery(id+"F0.wireOp",EDGE,"E29"),sQuery(id+"F0.wireOp",EDGE,"E30"),sQuery(id+"F0.wireOp",EDGE,"E31"),sQuery(id+"F0.wireOp",EDGE,"E32"),sQuery(id+"F0.wireOp",EDGE,"E33"),subQ0,sQuery(id+"F0.wireOp",EDGE,"E35"),sQuery(id+"F0.wireOp",EDGE,"E36.MirrorCS"),sQuery(id+"F0.wireOp",EDGE,"E37.MirrorCS"),sQuery(id+"F0.wireOp",EDGE,"E38.MirrorCS"),sQuery(id+"F0.wireOp",EDGE,"E39.MirrorCS"),sQuery(id+"F0.wireOp",EDGE,"E40.MirrorCS"),sQuery(id+"F0.wireOp",EDGE,"E46"),sQuery(id+"F0.wireOp",EDGE,"E47")])],"isStart":true})]});}
            var Q10;
            {var subQ0=sQuery(id+"F0.wireOp",EDGE,"E40.MirrorCS");Q10=makeQuery(id+"F6.opChamfer","BLEND_EDGE",EDGE,{"blendedFrom":[makeQuery(id+"F5.opExtrude","CAP_EDGE",EDGE,{"disambiguationData":[OSD([subQ0])],"isStart":false}),makeQuery(id+"F5.opExtrude","CAP_FACE",FACE,{"disambiguationData":[OSD([sQuery(id+"F0.wireOp",EDGE,"E21"),sQuery(id+"F0.wireOp",EDGE,"E22.MirrorCS"),sQuery(id+"F0.wireOp",EDGE,"E29"),sQuery(id+"F0.wireOp",EDGE,"E30"),sQuery(id+"F0.wireOp",EDGE,"E31"),sQuery(id+"F0.wireOp",EDGE,"E32"),sQuery(id+"F0.wireOp",EDGE,"E33"),sQuery(id+"F0.wireOp",EDGE,"E34"),sQuery(id+"F0.wireOp",EDGE,"E35"),sQuery(id+"F0.wireOp",EDGE,"E36.MirrorCS"),sQuery(id+"F0.wireOp",EDGE,"E37.MirrorCS"),sQuery(id+"F0.wireOp",EDGE,"E38.MirrorCS"),sQuery(id+"F0.wireOp",EDGE,"E39.MirrorCS"),subQ0,sQuery(id+"F0.wireOp",EDGE,"E46"),sQuery(id+"F0.wireOp",EDGE,"E47")])],"isStart":true})],"blendedInto":[makeQuery(id+"F5.opExtrude","CAP_FACE",FACE,{"disambiguationData":[OSD([sQuery(id+"F0.wireOp",EDGE,"E21"),sQuery(id+"F0.wireOp",EDGE,"E22.MirrorCS"),sQuery(id+"F0.wireOp",EDGE,"E29"),sQuery(id+"F0.wireOp",EDGE,"E30"),sQuery(id+"F0.wireOp",EDGE,"E31"),sQuery(id+"F0.wireOp",EDGE,"E32"),sQuery(id+"F0.wireOp",EDGE,"E33"),sQuery(id+"F0.wireOp",EDGE,"E34"),sQuery(id+"F0.wireOp",EDGE,"E35"),sQuery(id+"F0.wireOp",EDGE,"E36.MirrorCS"),sQuery(id+"F0.wireOp",EDGE,"E37.MirrorCS"),sQuery(id+"F0.wireOp",EDGE,"E38.MirrorCS"),sQuery(id+"F0.wireOp",EDGE,"E39.MirrorCS"),subQ0,sQuery(id+"F0.wireOp",EDGE,"E46"),sQuery(id+"F0.wireOp",EDGE,"E47")])],"isStart":true})]});}
            var Q11;
            {var subQ0=sQuery(id+"F0.wireOp",EDGE,"E35");Q11=makeQuery(id+"F6.opChamfer","BLEND_EDGE",EDGE,{"blendedFrom":[makeQuery(id+"F5.opExtrude","CAP_EDGE",EDGE,{"disambiguationData":[OSD([subQ0])],"isStart":false}),makeQuery(id+"F5.opExtrude","CAP_FACE",FACE,{"disambiguationData":[OSD([sQuery(id+"F0.wireOp",EDGE,"E21"),sQuery(id+"F0.wireOp",EDGE,"E22.MirrorCS"),sQuery(id+"F0.wireOp",EDGE,"E29"),sQuery(id+"F0.wireOp",EDGE,"E30"),sQuery(id+"F0.wireOp",EDGE,"E31"),sQuery(id+"F0.wireOp",EDGE,"E32"),sQuery(id+"F0.wireOp",EDGE,"E33"),sQuery(id+"F0.wireOp",EDGE,"E34"),subQ0,sQuery(id+"F0.wireOp",EDGE,"E36.MirrorCS"),sQuery(id+"F0.wireOp",EDGE,"E37.MirrorCS"),sQuery(id+"F0.wireOp",EDGE,"E38.MirrorCS"),sQuery(id+"F0.wireOp",EDGE,"E39.MirrorCS"),sQuery(id+"F0.wireOp",EDGE,"E40.MirrorCS"),sQuery(id+"F0.wireOp",EDGE,"E46"),sQuery(id+"F0.wireOp",EDGE,"E47")])],"isStart":true})],"blendedInto":[makeQuery(id+"F5.opExtrude","CAP_FACE",FACE,{"disambiguationData":[OSD([sQuery(id+"F0.wireOp",EDGE,"E21"),sQuery(id+"F0.wireOp",EDGE,"E22.MirrorCS"),sQuery(id+"F0.wireOp",EDGE,"E29"),sQuery(id+"F0.wireOp",EDGE,"E30"),sQuery(id+"F0.wireOp",EDGE,"E31"),sQuery(id+"F0.wireOp",EDGE,"E32"),sQuery(id+"F0.wireOp",EDGE,"E33"),sQuery(id+"F0.wireOp",EDGE,"E34"),subQ0,sQuery(id+"F0.wireOp",EDGE,"E36.MirrorCS"),sQuery(id+"F0.wireOp",EDGE,"E37.MirrorCS"),sQuery(id+"F0.wireOp",EDGE,"E38.MirrorCS"),sQuery(id+"F0.wireOp",EDGE,"E39.MirrorCS"),sQuery(id+"F0.wireOp",EDGE,"E40.MirrorCS"),sQuery(id+"F0.wireOp",EDGE,"E46"),sQuery(id+"F0.wireOp",EDGE,"E47")])],"isStart":true})]});}
            chamfer(context, id + "F7", {"entities" : qUnion([Q0, Q1, Q2, Q3, Q4, Q5, Q6, Q7, Q8, Q9, Q10, Q11]), "width" : 2.54 * mm, "tangentPropagation" : true});
        }
        {
            var Q0;
            Q0=makeQuery(id+"F2.opExtrude","CAP_EDGE",EDGE,{"disambiguationData":[OSD([sQuery(id+"F0.wireOp",EDGE,"E20")])],"isStart":false});
            var Q1;
            Q1=makeQuery(id+"F2.opExtrude","CAP_EDGE",EDGE,{"disambiguationData":[OSD([sQuery(id+"F0.wireOp",EDGE,"E23.MirrorCS")])],"isStart":false});
            var Q2;
            Q2=makeQuery(id+"F2.opExtrude","CAP_EDGE",EDGE,{"disambiguationData":[OSD([sQuery(id+"F0.wireOp",EDGE,"E28.MirrorCS")])],"isStart":false});
            var Q3;
            Q3=makeQuery(id+"F2.opExtrude","CAP_EDGE",EDGE,{"disambiguationData":[OSD([sQuery(id+"F0.wireOp",EDGE,"E19")])],"isStart":false});
            fillet(context, id + "F8", {"entities" : qUnion([Q0, Q1, Q2, Q3]), "radius" : 3.68 * mm, "tangentPropagation" : true, "allowEdgeOverflow" : false});
        }
        {
            var Q0;
            Q0=makeQuery(id+"F2.opExtrude","CAP_EDGE",EDGE,{"disambiguationData":[OSD([sQuery(id+"F0.wireOp",EDGE,"E23.MirrorCS")])],"isStart":true});
            var Q1;
            Q1=makeQuery(id+"F2.opExtrude","CAP_EDGE",EDGE,{"disambiguationData":[OSD([sQuery(id+"F0.wireOp",EDGE,"E20")])],"isStart":true});
            var Q2;
            Q2=makeQuery(id+"F2.opExtrude","CAP_EDGE",EDGE,{"disambiguationData":[OSD([sQuery(id+"F0.wireOp",EDGE,"E28.MirrorCS")])],"isStart":true});
            var Q3;
            Q3=makeQuery(id+"F2.opExtrude","CAP_EDGE",EDGE,{"disambiguationData":[OSD([sQuery(id+"F0.wireOp",EDGE,"E19")])],"isStart":true});
            fillet(context, id + "F9", {"entities" : qUnion([Q0, Q1, Q2, Q3]), "radius" : 5.08 * mm, "tangentPropagation" : true, "allowEdgeOverflow" : false});
        }
        {
            var Q0;
            Q0=makeQuery(id+"F3.opExtrude","CAP_EDGE",EDGE,{"disambiguationData":[OSD([sQuery(id+"F0.wireOp",EDGE,"E47")])],"isStart":true});
            var Q1;
            Q1=makeQuery(id+"F3.opExtrude","CAP_EDGE",EDGE,{"disambiguationData":[OSD([sQuery(id+"F0.wireOp",EDGE,"E46")])],"isStart":true});
            chamfer(context, id + "F10", {"entities" : qUnion([Q0, Q1]), "width" : 1.52 * mm, "tangentPropagation" : true});
        }
    });
